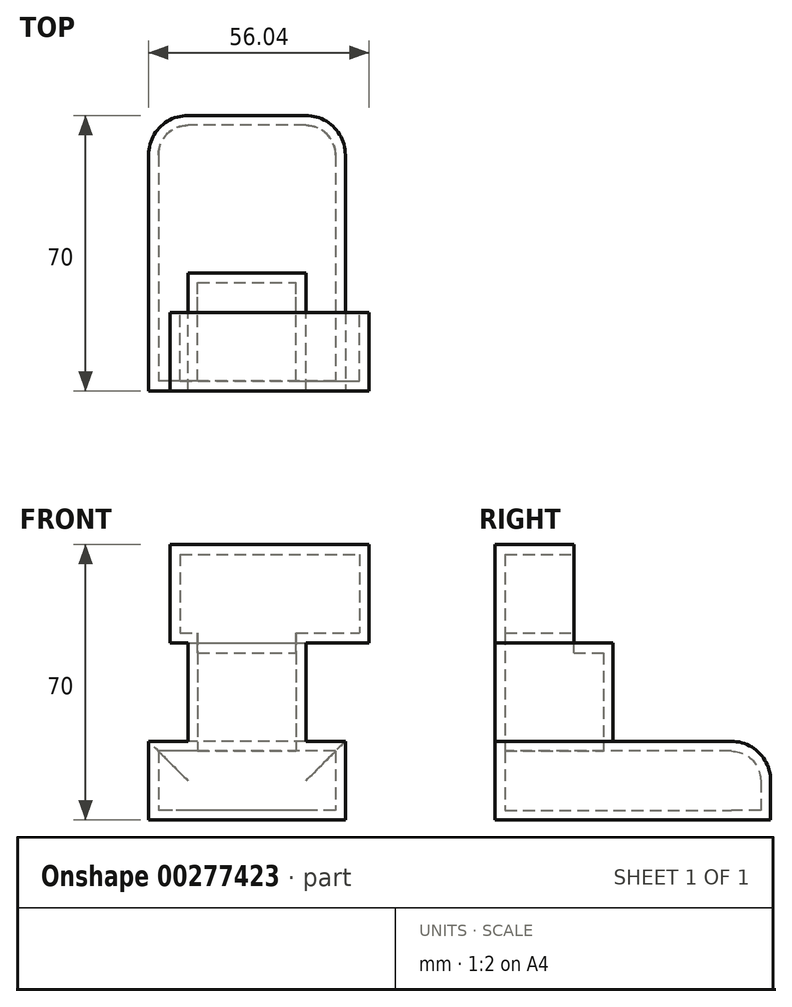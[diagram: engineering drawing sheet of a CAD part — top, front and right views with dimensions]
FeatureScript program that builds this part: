
annotation { "Feature Type Name" : "Feature", "Feature Type Description" : "" }
export const myFeature = defineFeature(function(context is Context, id is Id, definition is map)
    precondition{}
    {
        {
            var Q0;
            Q0=qCreatedBy(makeId("Right.planeOp"),FACE);
            var sketch = newSketch(context, id + "F0", { "sketchPlane" : qUnion([Q0])});
            skLineSegment(sketch, "E0", {"start": v(0, 20) * mm, "end": v(0, 0) * mm});
            skLineSegment(sketch, "E1", {"start": v(0, 0) * mm, "end": v(70, 0) * mm});
            skLineSegment(sketch, "E2", {"start": v(70, 0) * mm, "end": v(70, 20) * mm});
            skLineSegment(sketch, "E3", {"start": v(70, 20) * mm, "end": v(0, 20) * mm});
            skSolve(sketch);
        }
        {
            var Q0;
            Q0 = qSketchRegion(id + "F0", true);
            extrude(context, id + "F1", {"entities" : qUnion([Q0]), "endBound" : BoundingType.SYMMETRIC, "depth" : 50 * mm});
        }
        {
            var Q0;
            Q0=makeQuery(id+"F1.opExtrude","SWEPT_FACE",FACE,{"disambiguationData":[OSD([sQuery(id+"F0.wireOp",EDGE,"E3")])]});
            var sketch = newSketch(context, id + "F2", { "sketchPlane" : qUnion([Q0])});
            skLineSegment(sketch, "E4.bottom", {"start": v(-15, 0) * mm, "end": v(15, 0) * mm});
            skLineSegment(sketch, "E4.top", {"start": v(-15, 30) * mm, "end": v(15, 30) * mm});
            skLineSegment(sketch, "E4.left", {"start": v(-15, 0) * mm, "end": v(-15, 30) * mm});
            skLineSegment(sketch, "E4.right", {"start": v(15, 0) * mm, "end": v(15, 30) * mm});
            skSolve(sketch);
        }
        {
            var Q0;
            Q0 = qSketchRegion(id + "F2", true);
            extrude(context, id + "F3", {"entities" : qUnion([Q0]), "operationType" : NewBodyOperationType.ADD, "depth" : 25 * mm});
        }
        {
            var Q0;
            Q0=makeQuery(id+"F1.opExtrude","CAP_EDGE",EDGE,{"disambiguationData":[OSD([sQuery(id+"F0.wireOp",EDGE,"E2")])],"isStart":true});
            var Q1;
            Q1=makeQuery(id+"F1.opExtrude","SWEPT_EDGE",EDGE,{"disambiguationData":[OSD([sQuery(id+"F0.wireOp",EDGE,"E2"),sQuery(id+"F0.wireOp",EDGE,"E3")])]});
            var Q2;
            Q2=makeQuery(id+"F1.opExtrude","CAP_EDGE",EDGE,{"disambiguationData":[OSD([sQuery(id+"F0.wireOp",EDGE,"E2")])],"isStart":false});
            fillet(context, id + "F4", {"entities" : qUnion([Q0, Q1, Q2]), "radius" : 10 * mm, "tangentPropagation" : true, "allowEdgeOverflow" : false});
        }
        {
            var Q0;
            Q0=makeQuery(id+"F3.opExtrude","CAP_FACE",FACE,{"disambiguationData":[OSD([sQuery(id+"F2.wireOp",EDGE,"E4.bottom"),sQuery(id+"F2.wireOp",EDGE,"E4.top"),sQuery(id+"F2.wireOp",EDGE,"E4.left"),sQuery(id+"F2.wireOp",EDGE,"E4.right")])],"isStart":false});
            var sketch = newSketch(context, id + "F5", { "sketchPlane" : qUnion([Q0])});
            skLineSegment(sketch, "E5.bottom", {"start": v(-19.47, 0) * mm, "end": v(31.04, 0) * mm});
            skLineSegment(sketch, "E5.top", {"start": v(-19.47, 20) * mm, "end": v(31.04, 20) * mm});
            skLineSegment(sketch, "E5.left", {"start": v(-19.47, 0) * mm, "end": v(-19.47, 20) * mm});
            skLineSegment(sketch, "E5.right", {"start": v(31.04, 0) * mm, "end": v(31.04, 20) * mm});
            skSolve(sketch);
        }
        {
            var Q0;
            Q0 = qSketchRegion(id + "F5", true);
            extrude(context, id + "F6", {"entities" : qUnion([Q0]), "operationType" : NewBodyOperationType.ADD, "depth" : 25 * mm});
        }
        {
            var Q0;
            Q0=makeQuery(id+"F6.opExtrude","SWEPT_FACE",FACE,{"disambiguationData":[OSD([sQuery(id+"F5.wireOp",EDGE,"E5.top")])]});
            shell(context, id + "F7", {"entities" : qUnion([Q0]), "thickness" : 2.5 * mm});
        }
    });
